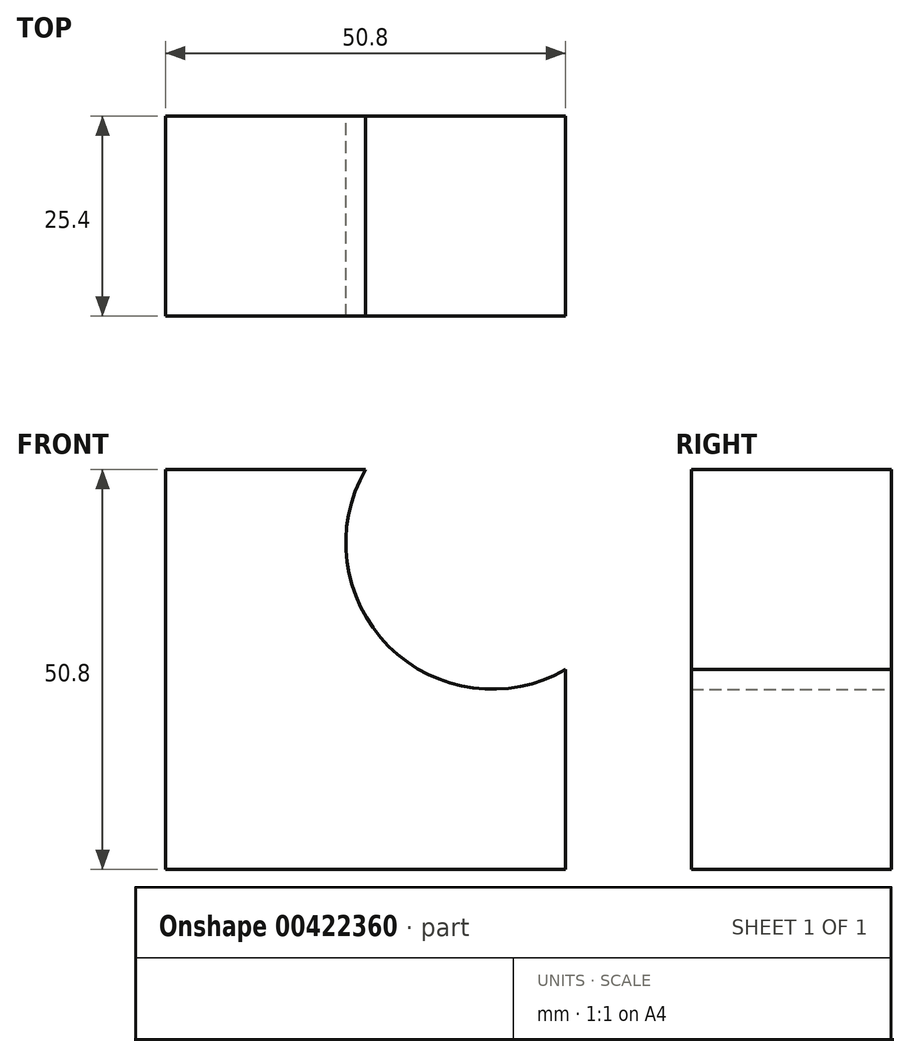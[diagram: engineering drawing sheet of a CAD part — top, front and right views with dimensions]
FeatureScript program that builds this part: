
annotation { "Feature Type Name" : "Feature", "Feature Type Description" : "" }
export const myFeature = defineFeature(function(context is Context, id is Id, definition is map)
    precondition{}
    {
        {
            var Q0;
            Q0=qCreatedBy(makeId("Front.planeOp"),FACE);
            var sketch = newSketch(context, id + "F0", { "sketchPlane" : qUnion([Q0])});
            skLineSegment(sketch, "E0", {"start": v(-50.8, 11.73) * mm, "end": v(-50.8, -39.07) * mm});
            skLineSegment(sketch, "E1", {"start": v(-50.8, -39.07) * mm, "end": v(0, -39.07) * mm});
            skLineSegment(sketch, "E2", {"start": v(0, -13.67) * mm, "end": v(0, -39.07) * mm});
            skLineSegment(sketch, "E3", {"start": v(-50.8, 11.73) * mm, "end": v(-25.4, 11.73) * mm});
            skPoint(sketch, "E4.endSnap0", {"position": v(-50.8, -13.67) * mm});
            skArc(sketch, "E5", {"start": v(-25.4, 11.73) * mm, "mid": v(-22.46, -10.73) * mm, "end": v(0, -13.67) * mm});
            skSolve(sketch);
        }
        {
            var Q0;
            Q0 = qSketchRegion(id + "F0", true);
            extrude(context, id + "F1", {"entities" : qUnion([Q0]), "depth" : 25.4 * mm});
        }
    });
